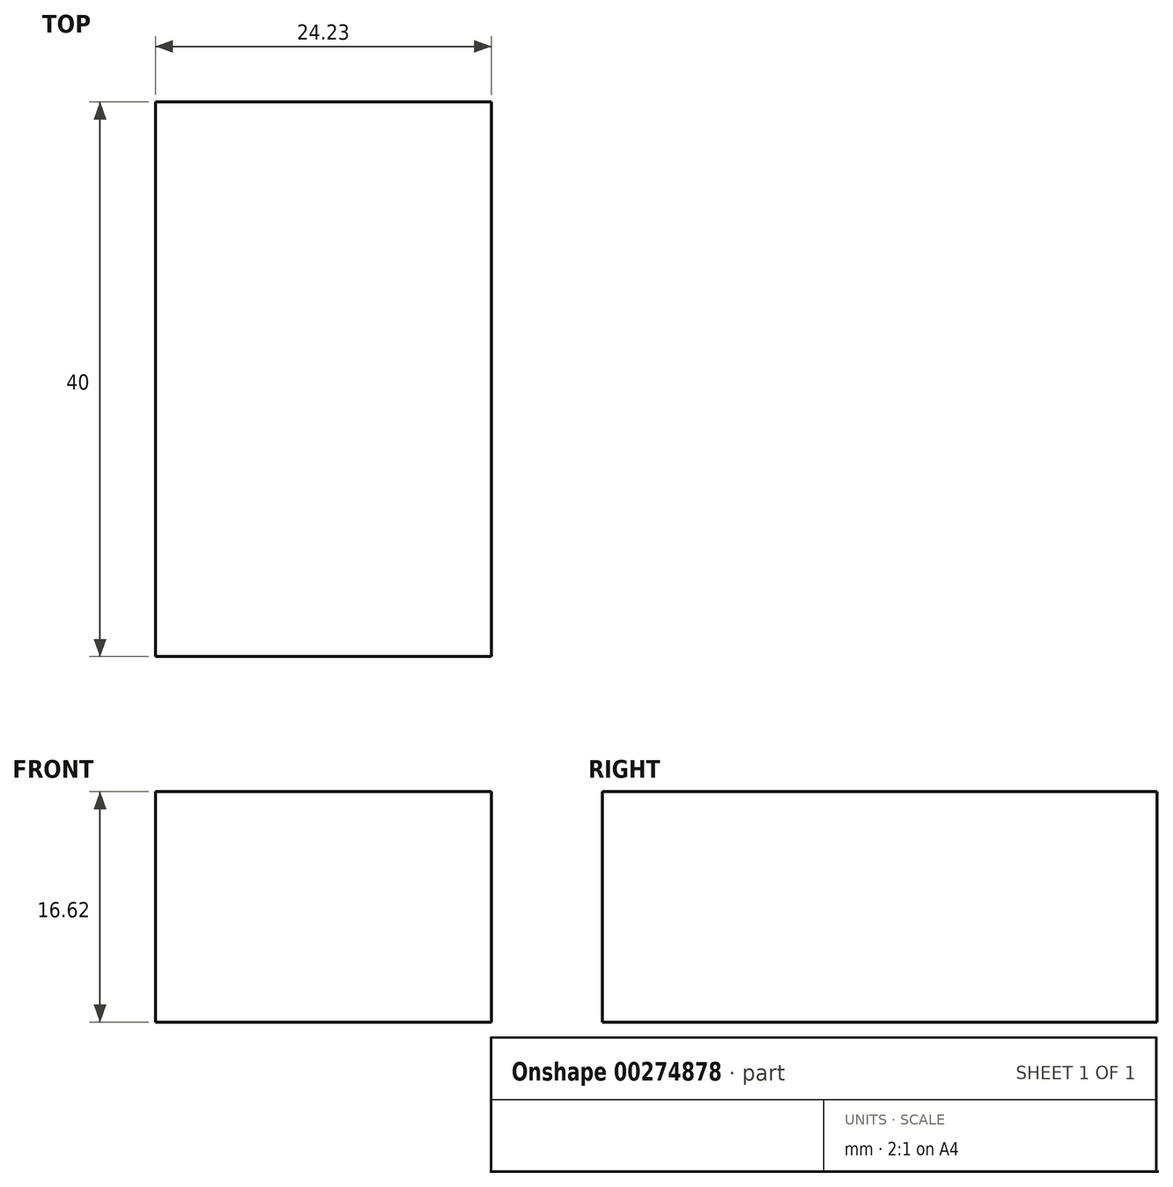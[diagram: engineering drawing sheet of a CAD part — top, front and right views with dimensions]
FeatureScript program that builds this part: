
annotation { "Feature Type Name" : "Feature", "Feature Type Description" : "" }
export const myFeature = defineFeature(function(context is Context, id is Id, definition is map)
    precondition{}
    {
        {
            var Q0;
            Q0=qCreatedBy(makeId("Front.planeOp"),FACE);
            var sketch = newSketch(context, id + "F0", { "sketchPlane" : qUnion([Q0])});
            skLineSegment(sketch, "E0.bottom", {"start": v(33.13, -41.4) * mm, "end": v(57.36, -41.4) * mm});
            skLineSegment(sketch, "E0.top", {"start": v(33.13, -58.02) * mm, "end": v(57.36, -58.02) * mm});
            skLineSegment(sketch, "E0.left", {"start": v(33.13, -41.4) * mm, "end": v(33.13, -58.02) * mm});
            skLineSegment(sketch, "E0.right", {"start": v(57.36, -41.4) * mm, "end": v(57.36, -58.02) * mm});
            skSolve(sketch);
        }
        {
            var Q0;
            Q0=makeQuery(id+"F0.imprint","IMPRINT",FACE,{"disambiguationData":[TD([[makeQuery(id+"F0.imprint","IMPRINT",EDGE,{"derivedFrom":sQuery(id+"F0.wireOp",EDGE,"E0.bottom")}),-1.0]])]});
            var sketch = newSketch(context, id + "F5", { "sketchPlane" : qUnion([Q0])});
            skSolve(sketch);
        }
        {
            var Q0;
            Q0=makeQuery(id+"F5.imprint","IMPRINT",FACE,{"disambiguationData":[TD([[makeQuery(id+"F5.imprint","IMPRINT",EDGE,{"derivedFrom":makeQuery(id+"F0.imprint","IMPRINT",EDGE,{"derivedFrom":sQuery(id+"F0.wireOp",EDGE,"E0.bottom")})}),-1.0]])]});
            var sketch = newSketch(context, id + "F1", { "sketchPlane" : qUnion([Q0])});
            skSolve(sketch);
        }
        {
            var Q0;
            Q0=makeQuery(id+"F0.imprint","IMPRINT",FACE,{"disambiguationData":[TD([[makeQuery(id+"F0.imprint","IMPRINT",EDGE,{"derivedFrom":sQuery(id+"F0.wireOp",EDGE,"E0.bottom")}),-1.0]])]});
            extrude(context, id + "F6", {"entities" : qUnion([Q0]), "oppositeDirection" : true, "depth" : 40 * mm});
        }
    });
